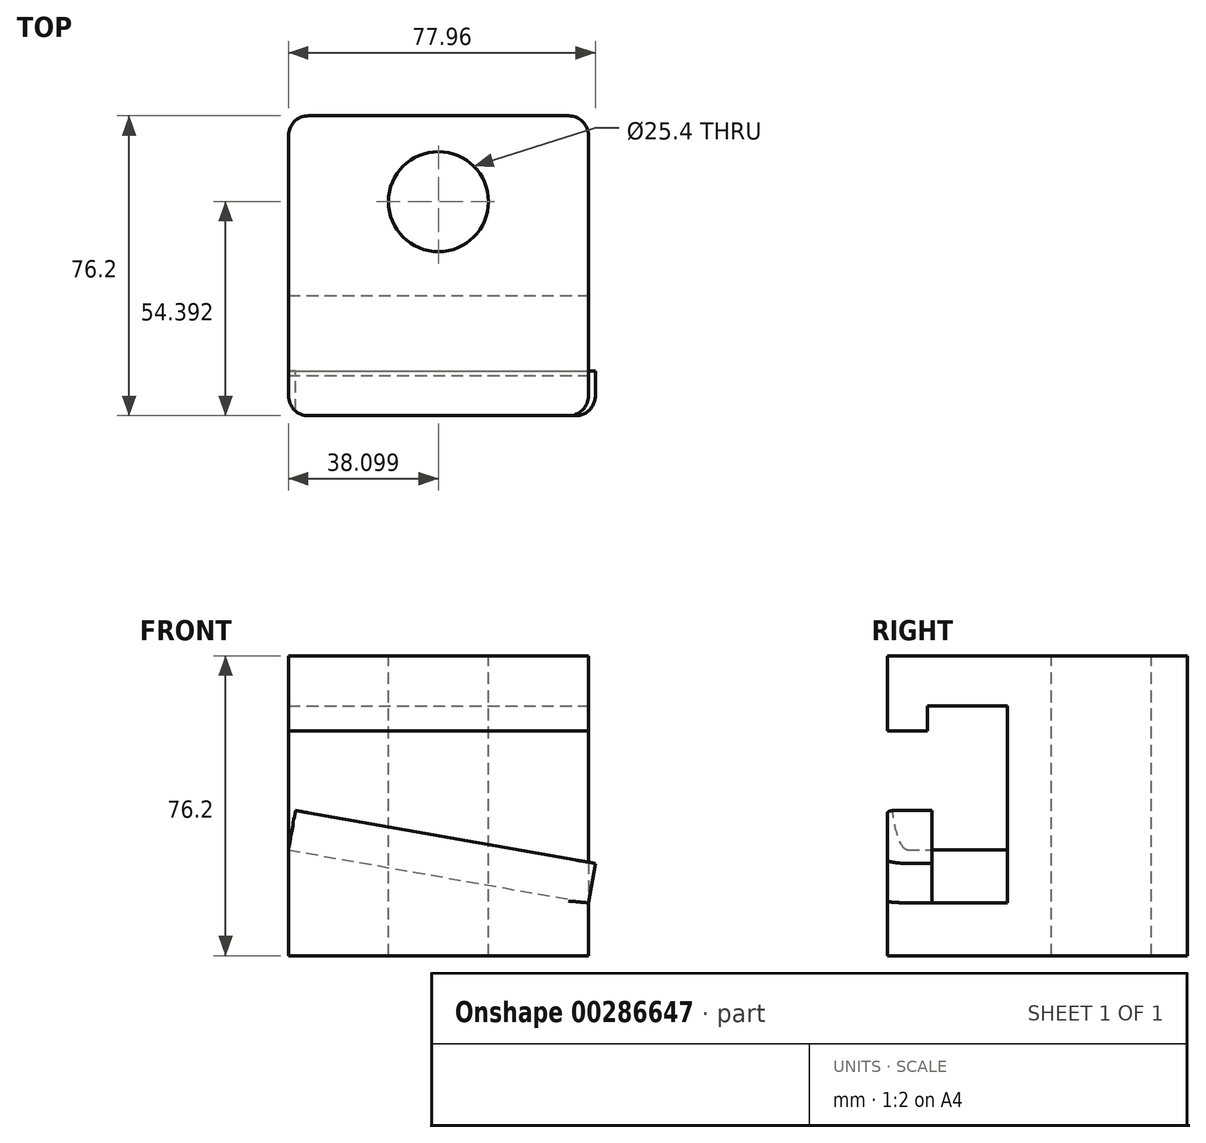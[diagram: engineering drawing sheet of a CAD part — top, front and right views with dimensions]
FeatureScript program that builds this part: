
annotation { "Feature Type Name" : "Feature", "Feature Type Description" : "" }
export const myFeature = defineFeature(function(context is Context, id is Id, definition is map)
    precondition{}
    {
        {
            var Q0;
            Q0=qCreatedBy(makeId("Front.planeOp"),FACE);
            var sketch = newSketch(context, id + "F0", { "sketchPlane" : qUnion([Q0])});
            skLineSegment(sketch, "E0.bottom", {"start": v(-30, 38.12) * mm, "end": v(46.2, 38.12) * mm});
            skLineSegment(sketch, "E0.top", {"start": v(-30, -38.08) * mm, "end": v(46.2, -38.08) * mm});
            skLineSegment(sketch, "E0.left", {"start": v(-30, 38.12) * mm, "end": v(-30, -38.08) * mm});
            skLineSegment(sketch, "E0.right", {"start": v(46.2, 38.12) * mm, "end": v(46.2, -38.08) * mm});
            skSolve(sketch);
        }
        {
            var Q0;
            Q0=makeQuery(id+"F0.imprint","IMPRINT",FACE,{"disambiguationData":[TD([[makeQuery(id+"F0.imprint","IMPRINT",EDGE,{"derivedFrom":sQuery(id+"F0.wireOp",EDGE,"E0.bottom")}),-1.0]])]});
            extrude(context, id + "F1", {"entities" : qUnion([Q0]), "depth" : 45.72 * mm});
        }
        {
            var Q0;
            Q0=makeQuery(id+"F1.opExtrude","CAP_FACE",FACE,{"disambiguationData":[OSD([sQuery(id+"F0.wireOp",EDGE,"E0.bottom"),sQuery(id+"F0.wireOp",EDGE,"E0.top"),sQuery(id+"F0.wireOp",EDGE,"E0.left"),sQuery(id+"F0.wireOp",EDGE,"E0.right")])],"isStart":false});
            var sketch = newSketch(context, id + "F2", { "sketchPlane" : qUnion([Q0])});
            skLineSegment(sketch, "E1", {"start": v(-30, 38.12) * mm, "end": v(-30, 25.42) * mm});
            skLineSegment(sketch, "E2", {"start": v(-30, 25.42) * mm, "end": v(46.2, 25.42) * mm});
            skLineSegment(sketch, "E3", {"start": v(46.2, 25.42) * mm, "end": v(46.2, 38.12) * mm});
            skLineSegment(sketch, "E4", {"start": v(46.2, 38.12) * mm, "end": v(-30, 38.12) * mm});
            skSolve(sketch);
        }
        {
            var Q0;
            Q0=makeQuery(id+"F2.imprint","IMPRINT",FACE,{"disambiguationData":[TD([[makeQuery(id+"F2.imprint","IMPRINT",EDGE,{"derivedFrom":sQuery(id+"F2.wireOp",EDGE,"E1")}),1.0]])]});
            extrude(context, id + "F3", {"entities" : qUnion([Q0]), "operationType" : NewBodyOperationType.ADD, "depth" : 30.48 * mm});
        }
        {
            var Q0;
            Q0=makeQuery(id+"F3.opExtrude","SWEPT_FACE",FACE,{"disambiguationData":[OSD([sQuery(id+"F2.wireOp",EDGE,"E2")])]});
            var sketch = newSketch(context, id + "F4", { "sketchPlane" : qUnion([Q0])});
            skLineSegment(sketch, "E5", {"start": v(-30, 76.2) * mm, "end": v(-30, 66.04) * mm});
            skLineSegment(sketch, "E6", {"start": v(-30, 66.04) * mm, "end": v(46.2, 66.04) * mm});
            skLineSegment(sketch, "E7", {"start": v(46.2, 66.04) * mm, "end": v(46.2, 76.2) * mm});
            skLineSegment(sketch, "E8", {"start": v(46.2, 76.2) * mm, "end": v(-30, 76.2) * mm});
            skSolve(sketch);
        }
        {
            var Q0;
            Q0=makeQuery(id+"F4.imprint","IMPRINT",FACE,{"disambiguationData":[TD([[makeQuery(id+"F4.imprint","IMPRINT",EDGE,{"derivedFrom":sQuery(id+"F4.wireOp",EDGE,"E5")}),1.0]])]});
            extrude(context, id + "F5", {"entities" : qUnion([Q0]), "operationType" : NewBodyOperationType.ADD, "depth" : 6.35 * mm});
        }
        {
            var Q0;
            Q0=makeQuery(id+"F1.opExtrude","CAP_FACE",FACE,{"disambiguationData":[OSD([sQuery(id+"F0.wireOp",EDGE,"E0.bottom"),sQuery(id+"F0.wireOp",EDGE,"E0.top"),sQuery(id+"F0.wireOp",EDGE,"E0.left"),sQuery(id+"F0.wireOp",EDGE,"E0.right")])],"isStart":false});
            var sketch = newSketch(context, id + "F6", { "sketchPlane" : qUnion([Q0])});
            skLineSegment(sketch, "E9", {"start": v(-30, -38.08) * mm, "end": v(-30, -11.2) * mm});
            skLineSegment(sketch, "E10", {"start": v(-30, -11.2) * mm, "end": v(46.2, -24.63) * mm});
            skLineSegment(sketch, "E11", {"start": v(46.2, -24.63) * mm, "end": v(46.2, -38.08) * mm});
            skLineSegment(sketch, "E12", {"start": v(46.2, -38.08) * mm, "end": v(-30, -38.08) * mm});
            skSolve(sketch);
        }
        {
            var Q0;
            Q0=makeQuery(id+"F6.imprint","IMPRINT",FACE,{"disambiguationData":[TD([[makeQuery(id+"F6.imprint","IMPRINT",EDGE,{"derivedFrom":sQuery(id+"F6.wireOp",EDGE,"E9")}),1.0]])]});
            extrude(context, id + "F7", {"entities" : qUnion([Q0]), "operationType" : NewBodyOperationType.ADD, "depth" : 30.48 * mm});
        }
        {
            var Q0;
            Q0=makeQuery(id+"F7.opExtrude","SWEPT_FACE",FACE,{"disambiguationData":[OSD([sQuery(id+"F6.wireOp",EDGE,"E10")])]});
            var sketch = newSketch(context, id + "F8", { "sketchPlane" : qUnion([Q0])});
            skLineSegment(sketch, "E13", {"start": v(-27.6, -76.2) * mm, "end": v(-27.6, -64.83) * mm});
            skLineSegment(sketch, "E14", {"start": v(-27.6, -64.83) * mm, "end": v(49.78, -64.83) * mm});
            skPoint(sketch, "E14.endSnap0", {"position": v(49.78, -60.96) * mm});
            skLineSegment(sketch, "E15", {"start": v(49.78, -64.83) * mm, "end": v(49.78, -76.2) * mm});
            skLineSegment(sketch, "E16", {"start": v(49.78, -76.2) * mm, "end": v(-27.6, -76.2) * mm});
            skSolve(sketch);
        }
        {
            var Q0;
            Q0=makeQuery(id+"F8.imprint","IMPRINT",FACE,{"disambiguationData":[TD([[makeQuery(id+"F8.imprint","IMPRINT",EDGE,{"derivedFrom":sQuery(id+"F8.wireOp",EDGE,"E13")}),-1.0]])]});
            extrude(context, id + "F9", {"entities" : qUnion([Q0]), "operationType" : NewBodyOperationType.ADD, "depth" : 10.16 * mm});
        }
        {
            var Q0;
            Q0=makeQuery(id+"F5.boolean.opBoolean","MERGE",EDGE,{"derivedFrom":[makeQuery(id+"F3.opExtrude","CAP_EDGE",EDGE,{"disambiguationData":[OSD([sQuery(id+"F2.wireOp",EDGE,"E1")])],"isStart":false}),makeQuery(id+"F5.opExtrude","SWEPT_EDGE",EDGE,{"disambiguationData":[OSD([sQuery(id+"F4.wireOp",EDGE,"E5"),sQuery(id+"F4.wireOp",EDGE,"E8")])]})]});
            var Q1;
            Q1=makeQuery(id+"F7.opExtrude","CAP_EDGE",EDGE,{"disambiguationData":[OSD([sQuery(id+"F6.wireOp",EDGE,"E9")])],"isStart":false});
            var Q2;
            Q2=makeQuery(id+"F7.opExtrude","CAP_EDGE",EDGE,{"disambiguationData":[OSD([sQuery(id+"F6.wireOp",EDGE,"E11")])],"isStart":false});
            var Q3;
            Q3=makeQuery(id+"F9.opExtrude","SWEPT_EDGE",EDGE,{"disambiguationData":[OSD([sQuery(id+"F8.wireOp",EDGE,"E15"),sQuery(id+"F8.wireOp",EDGE,"E16")])]});
            var Q4;
            Q4=makeQuery(id+"F5.boolean.opBoolean","MERGE",EDGE,{"derivedFrom":[makeQuery(id+"F3.opExtrude","CAP_EDGE",EDGE,{"disambiguationData":[OSD([sQuery(id+"F2.wireOp",EDGE,"E3")])],"isStart":false}),makeQuery(id+"F5.opExtrude","SWEPT_EDGE",EDGE,{"disambiguationData":[OSD([sQuery(id+"F4.wireOp",EDGE,"E7"),sQuery(id+"F4.wireOp",EDGE,"E8")])]})]});
            var Q5;
            Q5=makeQuery(id+"F1.opExtrude","CAP_EDGE",EDGE,{"disambiguationData":[OSD([sQuery(id+"F0.wireOp",EDGE,"E0.right")])],"isStart":true});
            var Q6;
            Q6=makeQuery(id+"F1.opExtrude","CAP_EDGE",EDGE,{"disambiguationData":[OSD([sQuery(id+"F0.wireOp",EDGE,"E0.left")])],"isStart":true});
            fillet(context, id + "F10", {"entities" : qUnion([Q0, Q1, Q2, Q3, Q4, Q5, Q6]), "radius" : 5.08 * mm, "tangentPropagation" : true, "allowEdgeOverflow" : false});
        }
        {
            var Q0;
            Q0=makeQuery(id+"F3.boolean.opBoolean","MERGE",FACE,{"derivedFrom":[makeQuery(id+"F1.opExtrude","SWEPT_FACE",FACE,{"disambiguationData":[OSD([sQuery(id+"F0.wireOp",EDGE,"E0.bottom")])]}),makeQuery(id+"F3.opExtrude","SWEPT_FACE",FACE,{"disambiguationData":[OSD([sQuery(id+"F2.wireOp",EDGE,"E4")])]})]});
            var sketch = newSketch(context, id + "F11", { "sketchPlane" : qUnion([Q0])});
            skCircle(sketch, "E17", {"center": v(8.1, -21.8) * mm, "radius": 12.7 * mm});
            skSolve(sketch);
        }
        {
            var Q0;
            Q0=sQuery(id+"F11.wireOp",VERTEX,"E17.center");
            var Q1;
            Q1=makeQuery(id+"F1.opExtrude","SWEPT_BODY",BODY,{"disambiguationData":[OSD([sQuery(id+"F0.wireOp",EDGE,"E0.bottom"),sQuery(id+"F0.wireOp",EDGE,"E0.top"),sQuery(id+"F0.wireOp",EDGE,"E0.left"),sQuery(id+"F0.wireOp",EDGE,"E0.right")])]});
            hole(context, id + "F12", {"style" : HoleStyle.SIMPLE, "endStyle" : HoleEndStyle.THROUGH, "holeDiameter" : 25.4 * mm, "tappedDepth" : 12.7 * mm, "tapClearance" : 3, "locations" : qUnion([Q0]), "scope" : qUnion([Q1])});
        }
    });
